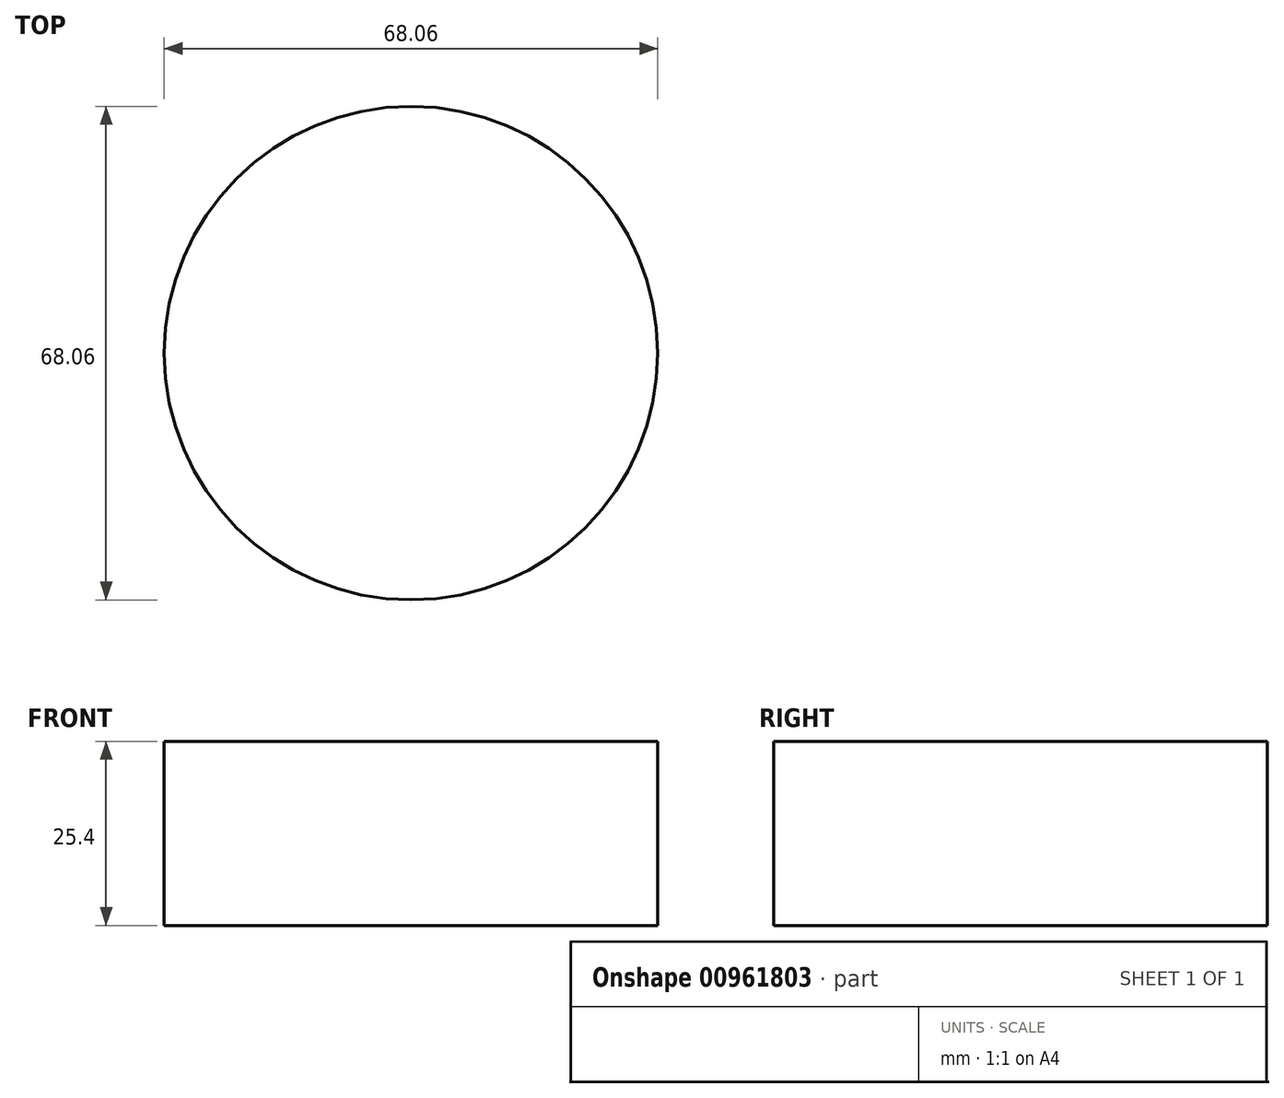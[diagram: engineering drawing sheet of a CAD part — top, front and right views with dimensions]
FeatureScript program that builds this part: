
annotation { "Feature Type Name" : "Feature", "Feature Type Description" : "" }
export const myFeature = defineFeature(function(context is Context, id is Id, definition is map)
    precondition{}
    {
        {
            var Q0;
            Q0=qCreatedBy(makeId("Top.planeOp"),FACE);
            var sketch = newSketch(context, id + "F0", { "sketchPlane" : qUnion([Q0])});
            skCircle(sketch, "E0", {"center": v(0, 0) * mm, "radius": 34.03 * mm});
            skSolve(sketch);
        }
        {
            var Q0;
            Q0 = qSketchRegion(id + "F0", true);
            extrude(context, id + "F1", {"entities" : qUnion([Q0]), "depth" : 25.4 * mm, "offsetDistance" : 25.4 * mm});
        }
    });
